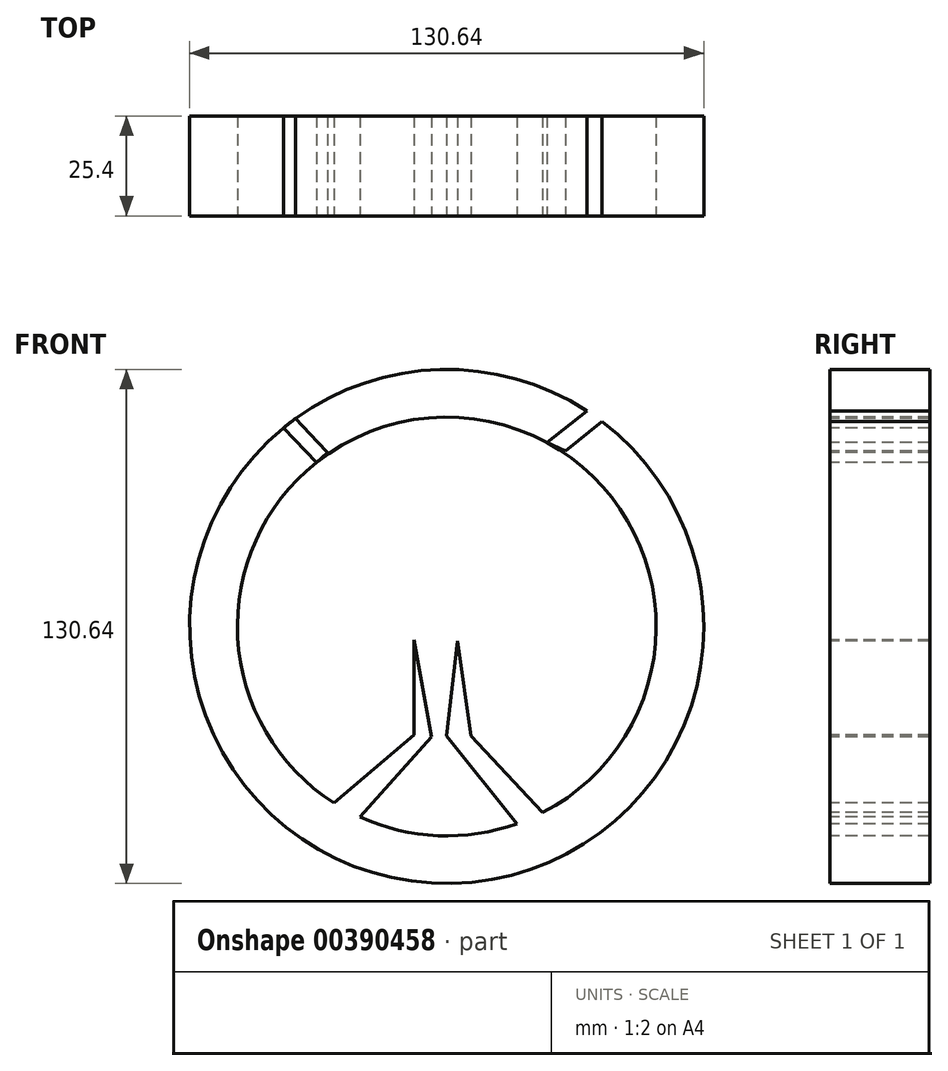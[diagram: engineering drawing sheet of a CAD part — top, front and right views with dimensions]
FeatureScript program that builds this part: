
annotation { "Feature Type Name" : "Feature", "Feature Type Description" : "" }
export const myFeature = defineFeature(function(context is Context, id is Id, definition is map)
    precondition{}
    {
        {
            var Q0;
            Q0=qCreatedBy(makeId("Front.planeOp"),FACE);
            var sketch = newSketch(context, id + "F0", { "sketchPlane" : qUnion([Q0])});
            skCircle(sketch, "E0", {"center": v(0, 0) * mm, "radius": 65.32 * mm});
            skSolve(sketch);
        }
        {
            var Q0;
            Q0 = qSketchRegion(id + "F0", true);
            extrude(context, id + "F1", {"entities" : qUnion([Q0]), "depth" : 25.4 * mm});
        }
        {
            var Q0;
            Q0=makeQuery(id+"F1.opExtrude","CAP_FACE",FACE,{"disambiguationData":[OSD([sQuery(id+"F0.wireOp",EDGE,"E0")])],"isStart":false});
            var sketch = newSketch(context, id + "F2", { "sketchPlane" : qUnion([Q0])});
            skLineSegment(sketch, "E1", {"start": v(-41.47, 50.46) * mm, "end": v(-35.6, 44.26) * mm});
            skLineSegment(sketch, "E2", {"start": v(-35.6, 44.26) * mm, "end": v(-32.82, 46.9) * mm});
            skLineSegment(sketch, "E3", {"start": v(-32.82, 46.9) * mm, "end": v(-38.42, 52.82) * mm});
            skLineSegment(sketch, "E4", {"start": v(-38.42, 52.82) * mm, "end": v(-41.47, 50.46) * mm});
            skLineSegment(sketch, "E5", {"start": v(35.59, 54.77) * mm, "end": v(30.22, 50.46) * mm});
            skLineSegment(sketch, "E6", {"start": v(30.22, 50.46) * mm, "end": v(33.07, 46.9) * mm});
            skLineSegment(sketch, "E7", {"start": v(33.07, 46.9) * mm, "end": v(39.48, 52.03) * mm});
            skSolve(sketch);
        }
        {
            var Q0;
            Q0=makeQuery(id+"F2.imprint","IMPRINT",FACE,{"disambiguationData":[TD([[makeQuery(id+"F2.imprint","IMPRINT",EDGE,{"derivedFrom":sQuery(id+"F2.wireOp",EDGE,"E1")}),1.0]])]});
            var Q1;
            {var subQ0=sQuery(id+"F2.wireOp",EDGE,"E5");Q1=makeQuery(id+"F2.imprint","IMPRINT",FACE,{"disambiguationData":[TD([[makeQuery(id+"F2.imprint","IMPRINT",EDGE,{"derivedFrom":subQ0}),1.0]])]});}
            extrude(context, id + "F3", {"entities" : qUnion([Q0, Q1]), "operationType" : NewBodyOperationType.REMOVE, "oppositeDirection" : true, "depth" : 25.4 * mm});
        }
        {
            var Q0;
            {var subQ0=sQuery(id+"F0.wireOp",EDGE,"E0");Q0=makeQuery(id+"F3.boolean.opBoolean","SPLIT",FACE,{"disambiguationData":[TD([makeQuery(id+"F3.opExtrude","SWEPT_FACE",FACE,{"disambiguationData":[OSD([sQuery(id+"F2.wireOp",EDGE,"E1")])]})])],"derivedFrom":makeQuery(id+"F1.opExtrude","CAP_FACE",FACE,{"disambiguationData":[OSD([subQ0])],"isStart":false})});}
            var sketch = newSketch(context, id + "F4", { "sketchPlane" : qUnion([Q0])});
            skCircle(sketch, "E8", {"center": v(0, 0) * mm, "radius": 53.2 * mm});
            skLineSegment(sketch, "E9", {"start": v(-28.6, -44.85) * mm, "end": v(-8.37, -27.52) * mm});
            skLineSegment(sketch, "E10", {"start": v(-8.37, -27.52) * mm, "end": v(-8.37, -3.4) * mm});
            skLineSegment(sketch, "E11", {"start": v(-8.37, -3.4) * mm, "end": v(-3.83, -28.09) * mm});
            skLineSegment(sketch, "E12", {"start": v(-3.83, -28.09) * mm, "end": v(-22.02, -48.43) * mm});
            skLineSegment(sketch, "E13", {"start": v(17.88, -50.1) * mm, "end": v(0, -27.8) * mm});
            skLineSegment(sketch, "E14", {"start": v(0, -27.8) * mm, "end": v(2.7, -3.69) * mm});
            skLineSegment(sketch, "E15", {"start": v(2.7, -3.69) * mm, "end": v(6.1, -27.8) * mm});
            skLineSegment(sketch, "E16", {"start": v(6.1, -27.8) * mm, "end": v(24.36, -47.3) * mm});
            skLineSegment(sketch, "E17", {"start": v(-22.02, -48.43) * mm, "end": v(-28.6, -44.85) * mm});
            skLineSegment(sketch, "E18", {"start": v(17.88, -50.1) * mm, "end": v(24.36, -47.3) * mm});
            skSolve(sketch);
        }
        {
            var Q0;
            {var subQ0=sQuery(id+"F4.wireOp",EDGE,"E9");Q0=makeQuery(id+"F4.imprint","IMPRINT",FACE,{"disambiguationData":[TD([[makeQuery(id+"F4.imprint","IMPRINT",EDGE,{"derivedFrom":subQ0}),1.0]])]});}
            extrude(context, id + "F5", {"entities" : qUnion([Q0]), "operationType" : NewBodyOperationType.REMOVE, "oppositeDirection" : true, "depth" : 25.4 * mm});
        }
        {
            var Q0;
            {var subQ0=sQuery(id+"F0.wireOp",EDGE,"E0");Q0=makeQuery(id+"F3.boolean.opBoolean","SPLIT",FACE,{"disambiguationData":[TD([makeQuery(id+"F3.opExtrude","SWEPT_FACE",FACE,{"disambiguationData":[OSD([sQuery(id+"F2.wireOp",EDGE,"E1")])]})])],"derivedFrom":makeQuery(id+"F1.opExtrude","CAP_FACE",FACE,{"disambiguationData":[OSD([subQ0])],"isStart":false})});}
            var sketch = newSketch(context, id + "F6", { "sketchPlane" : qUnion([Q0])});
            skLineSegment(sketch, "E19", {"start": v(-35.6, 44.26) * mm, "end": v(-33.12, 41.63) * mm});
            skLineSegment(sketch, "E20", {"start": v(-33.12, 41.63) * mm, "end": v(-30.34, 44.26) * mm});
            skLineSegment(sketch, "E21", {"start": v(-30.34, 44.26) * mm, "end": v(-32.82, 46.9) * mm});
            skLineSegment(sketch, "E22", {"start": v(30.22, 50.46) * mm, "end": v(25.5, 46.69) * mm});
            skLineSegment(sketch, "E23", {"start": v(25.5, 46.69) * mm, "end": v(33.07, 46.9) * mm});
            skLineSegment(sketch, "E24", {"start": v(33.07, 46.9) * mm, "end": v(30.22, 44.6) * mm});
            skLineSegment(sketch, "E25", {"start": v(30.22, 44.6) * mm, "end": v(25.5, 46.69) * mm});
            skSolve(sketch);
        }
        {
            var Q0;
            Q0=makeQuery(id+"F6.imprint","IMPRINT",FACE,{"disambiguationData":[TD([[makeQuery(id+"F6.imprint","IMPRINT",EDGE,{"derivedFrom":sQuery(id+"F6.wireOp",EDGE,"E19")}),1.0]])]});
            var Q1;
            Q1=makeQuery(id+"F6.imprint","IMPRINT",FACE,{"disambiguationData":[TD([[makeQuery(id+"F6.imprint","IMPRINT",EDGE,{"derivedFrom":sQuery(id+"F6.wireOp",EDGE,"E22")}),1.0]])]});
            var Q2;
            Q2=makeQuery(id+"F6.imprint","IMPRINT",FACE,{"disambiguationData":[TD([[makeQuery(id+"F6.imprint","IMPRINT",EDGE,{"derivedFrom":sQuery(id+"F6.wireOp",EDGE,"E23")}),-1.0]])]});
            extrude(context, id + "F7", {"entities" : qUnion([Q0, Q1, Q2]), "operationType" : NewBodyOperationType.REMOVE, "oppositeDirection" : true, "depth" : 25.4 * mm});
        }
        {
            var Q0;
            {var subQ6=sQuery(id+"F0.wireOp",EDGE,"E0");var subQ10=makeQuery(id+"F3.opExtrude","SWEPT_FACE",FACE,{"disambiguationData":[OSD([sQuery(id+"F2.wireOp",EDGE,"E1")])]});Q0=makeQuery(id+"F7.boolean.opBoolean","SPLIT",FACE,{"disambiguationData":[TD([makeQuery(id+"F3.boolean.opBoolean","COPY",FACE,{"derivedFrom":subQ10})])],"derivedFrom":makeQuery(id+"F3.boolean.opBoolean","SPLIT",FACE,{"disambiguationData":[TD([subQ10])],"derivedFrom":makeQuery(id+"F1.opExtrude","CAP_FACE",FACE,{"disambiguationData":[OSD([subQ6])],"isStart":false})})});}
            var sketch = newSketch(context, id + "F8", { "sketchPlane" : qUnion([Q0])});
            skLineSegment(sketch, "E26", {"start": v(30.22, 44.6) * mm, "end": v(28.8, 41.4) * mm});
            skLineSegment(sketch, "E27", {"start": v(28.8, 41.4) * mm, "end": v(25.5, 46.69) * mm});
            skLineSegment(sketch, "E28", {"start": v(-33.12, 41.63) * mm, "end": v(-29.08, 36.6) * mm});
            skLineSegment(sketch, "E29", {"start": v(-29.08, 36.6) * mm, "end": v(-29.08, 43.98) * mm});
            skSolve(sketch);
        }
        {
            var Q0;
            {var subQ0=sQuery(id+"F8.wireOp",EDGE,"E27");Q0=makeQuery(id+"F8.imprint","IMPRINT",FACE,{"disambiguationData":[TD([[makeQuery(id+"F8.imprint","IMPRINT",EDGE,{"derivedFrom":subQ0}),-1.0]])]});}
            extrude(context, id + "F9", {"entities" : qUnion([Q0]), "operationType" : NewBodyOperationType.REMOVE, "oppositeDirection" : true, "depth" : 25.4 * mm});
        }
    });
